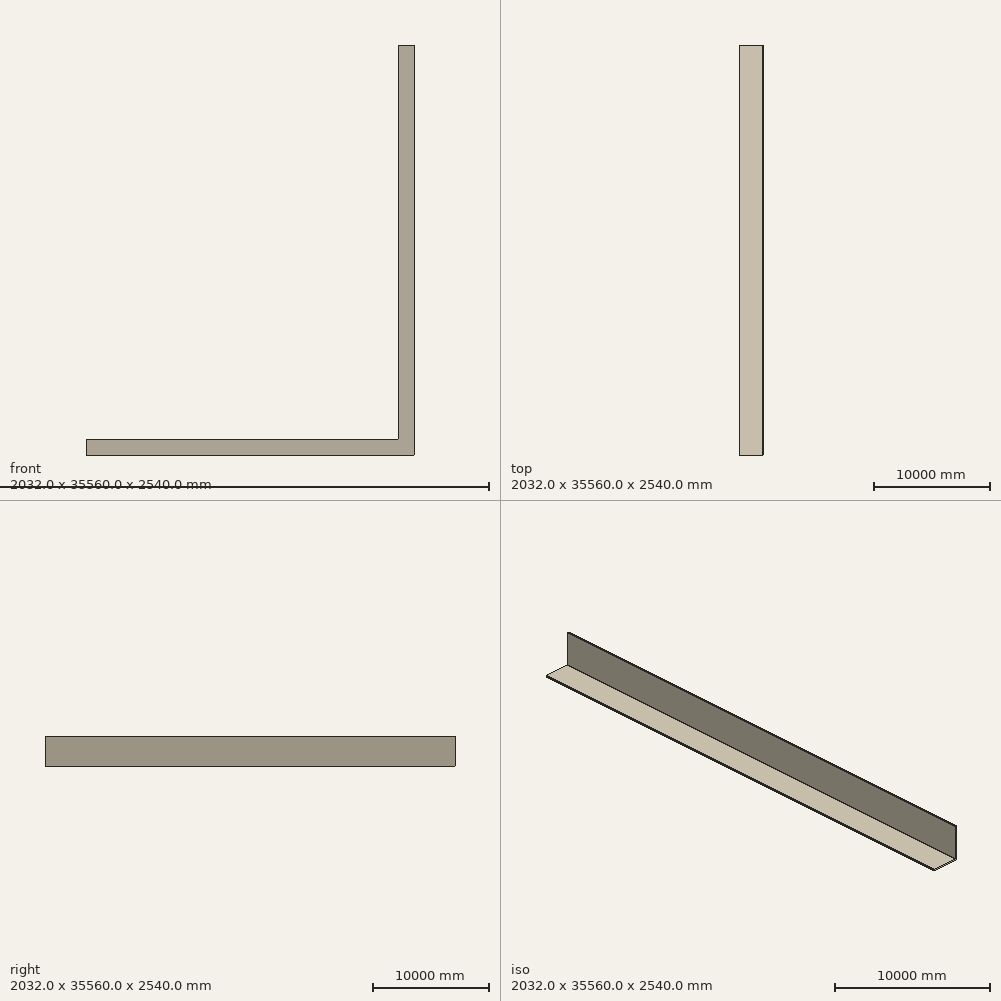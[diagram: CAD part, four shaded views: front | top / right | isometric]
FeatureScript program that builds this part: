
annotation { "Feature Type Name" : "Feature", "Feature Type Description" : "" }
export const myFeature = defineFeature(function(context is Context, id is Id, definition is map)
    precondition{}
    {
        {
            var Q0;
            Q0=qCreatedBy(makeId("Front.planeOp"),FACE);
            var sketch = newSketch(context, id + "F0", { "sketchPlane" : qUnion([Q0])});
            skLineSegment(sketch, "E0", {"start": v(0, 0) * mm, "end": v(2032, 0) * mm});
            skLineSegment(sketch, "E1", {"start": v(2032, 0) * mm, "end": v(2032, 2540) * mm});
            skLineSegment(sketch, "E2.0", {"start": v(1930.4, 101.6) * mm, "end": v(1930.4, 2540) * mm});
            skLineSegment(sketch, "E2.1", {"start": v(0, 101.6) * mm, "end": v(1930.4, 101.6) * mm});
            skLineSegment(sketch, "E3", {"start": v(0, 0) * mm, "end": v(0, 101.6) * mm});
            skLineSegment(sketch, "E4", {"start": v(1930.4, 2540) * mm, "end": v(2032, 2540) * mm});
            skSolve(sketch);
        }
        {
            var Q0;
            Q0 = qSketchRegion(id + "F0", true);
            extrude(context, id + "F1", {"entities" : qUnion([Q0]), "oppositeDirection" : true, "depth" : 35560 * mm, "offsetDistance" : 25.4 * mm});
        }
    });
